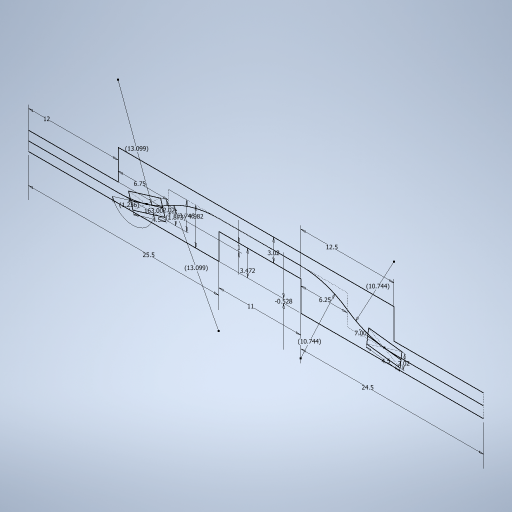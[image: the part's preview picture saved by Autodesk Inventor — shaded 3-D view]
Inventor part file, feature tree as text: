
AUTODESK INVENTOR PART (.ipt)
format: ipt  version: 2024 (Build 280153000, 153)  size: 278,016 bytes
history: native  units: in
note: dims shown in document units (in); Inventor stores cm internally (conversion verified against a paired STEP export)
features: sketch x1
ambient origin geometry x8: Origin, YZ Plane, XZ Plane, XY Plane, X Axis, Y Axis, Z Axis, Center Point
feature tree (1):
  sketch  "Sketch1"  dims[d0=1.0039in d1=0.4331in d2=0.9646in d3=-0.0208in d4=0.1367in d5=0.0394in d6=0.1189in d7=0.4724in d8=0.4921in d9=0.0487in d10=0.1961in d11=0.2657in d12=0.2461in d13=0.5157in d14=0.5157in d15=0.1772in d16=0.0795in d18=0.1168in d19=0.1475in d20=0.0737in d21=0.423in d22=0.423in d23=0.1772in d24=0.0795in d26=0.0481in]
